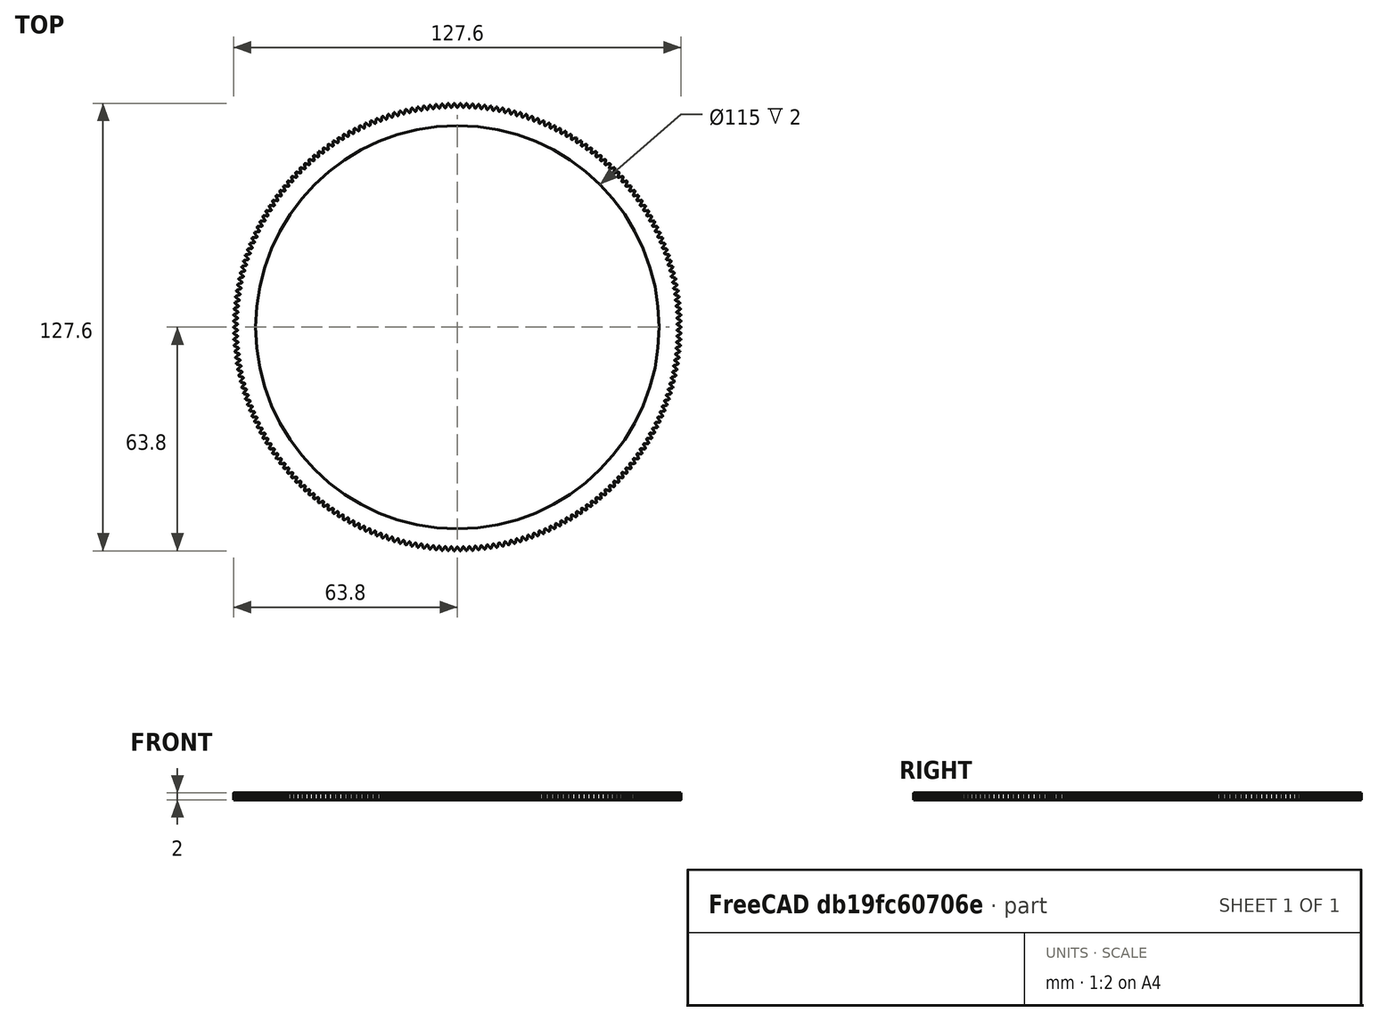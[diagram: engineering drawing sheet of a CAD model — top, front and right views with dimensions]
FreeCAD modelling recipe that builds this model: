
FCSTD DOCUMENT  (FreeCAD 1.0R39109 (Git))
Label: bass
License: All rights reserved
LicenseURL: https://en.wikipedia.org/wiki/All_rights_reserved
objects: Part::Part2DObjectPython×1, PartDesign::Pad×1, Sketcher::SketchObject×1, PartDesign::Pocket×1, PartDesign::Body×1
note: 10 computed .brp shape members not serialized (recipe doc carries the construction recipe); baked Part::Feature solids carry a one-line shape summary decoded from their .brp

FEATURE [Part::Part2DObjectPython] InvoluteGear  # Draft 2D object (typed FeaturePython)
  AddendumCoefficient = 1
  DedendumCoefficient = 1.25
  ExternalGear = true
  HighPrecision = true
  Modules = 0.55
  NumberOfTeeth = 230
  PressureAngle = 28
  ProfileShiftCoefficient = 0
  RootFilletCoefficient = 0.38
FEATURE [PartDesign::Pad] Pad
  Direction = (0,0,1)
  Length = 2
  Length2 = 10
  Profile = -> InvoluteGear
  ReferenceAxis = -> InvoluteGear [N_Axis]
  Refine = true
  Suppressed = false
  Type = 0
FEATURE [Sketcher::SketchObject] Sketch
  ArcFitTolerance = 1e-06
  AttachmentSupport = -> [Pad]
  FullyConstrained = true
  MakeInternals = false
  MapMode = 5
  Placement = pos=(0,0,2) rot=(0,0,1;0rad)
  sketch-geometry (1):
    g0: Circle CenterX=0 CenterY=0 CenterZ=0 NormalX=0 NormalY=0 NormalZ=1 AngleXU=0 Radius=57.5
  constraints (2):
    c: Diameter(g0) = 115
    c: Coincident(g0,g-1)
FEATURE [PartDesign::Pocket] Pocket
  BaseFeature = -> Pad
  Direction = (0,0,-1)
  Length = 5
  Length2 = 5
  Profile = -> Sketch
  ReferenceAxis = -> Sketch [N_Axis]
  Refine = true
  Suppressed = false
  Type = 1
FEATURE [PartDesign::Body] Body
  AllowCompound = false
  Group = -> [InvoluteGear,Pad,Sketch,Pocket]
  Origin = -> Origin
  Tip = -> Pocket
